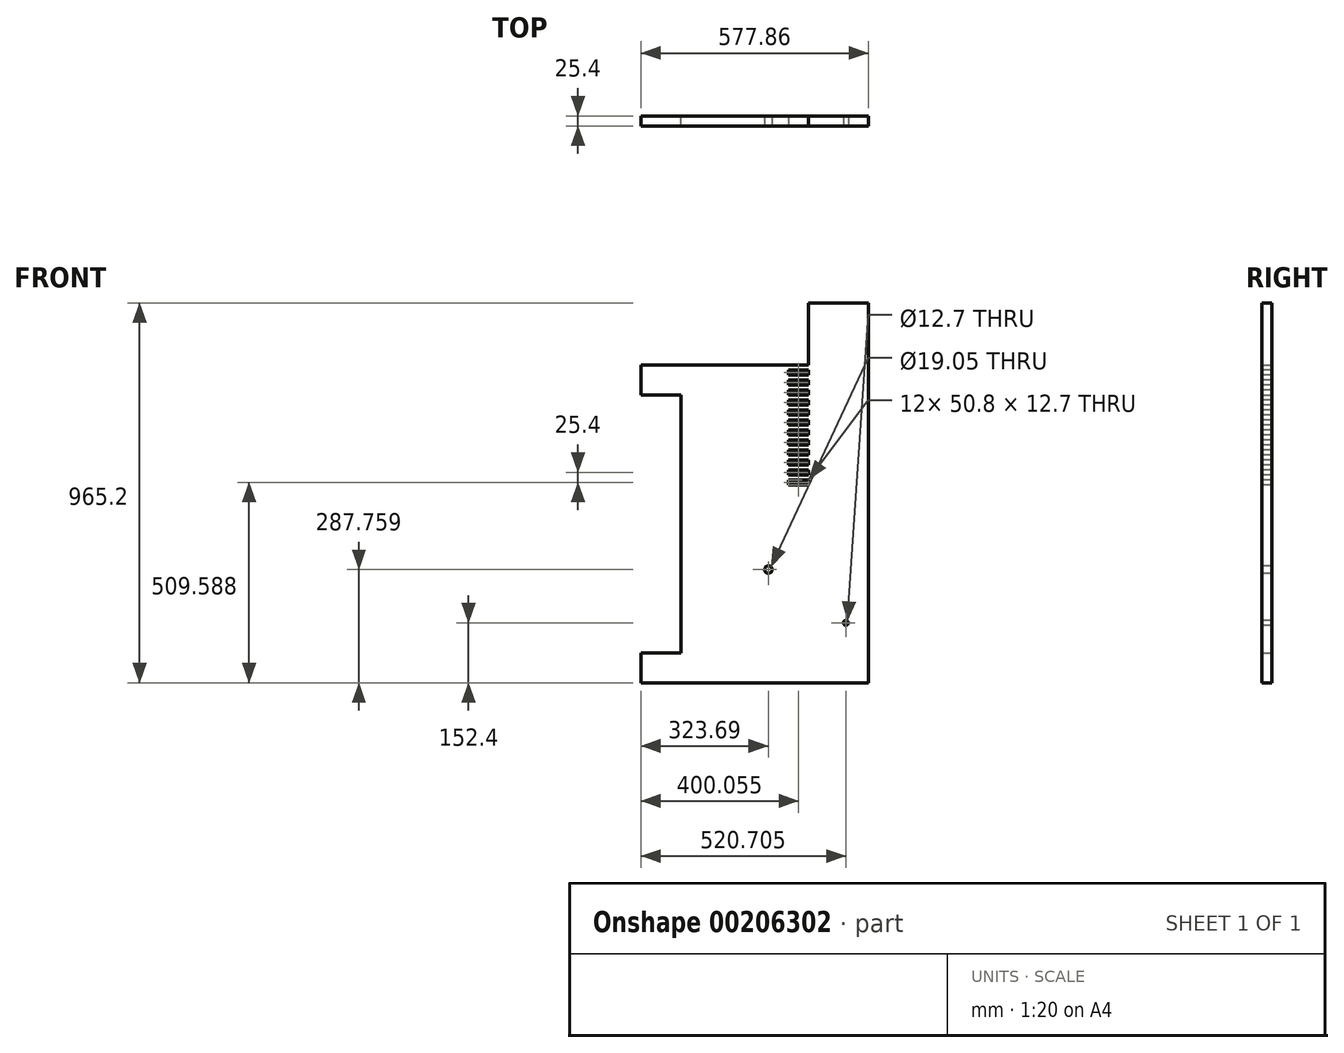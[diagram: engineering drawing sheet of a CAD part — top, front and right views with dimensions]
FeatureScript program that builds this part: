
annotation { "Feature Type Name" : "Feature", "Feature Type Description" : "" }
export const myFeature = defineFeature(function(context is Context, id is Id, definition is map)
    precondition{}
    {
        {
            var Q0;
            Q0=qCreatedBy(makeId("Front.planeOp"),FACE);
            var sketch = newSketch(context, id + "F0", { "sketchPlane" : qUnion([Q0])});
            skLineSegment(sketch, "E0.bottom", {"start": v(-288.93, 482.6) * mm, "end": v(288.93, 482.6) * mm, "construction": true});
            skLineSegment(sketch, "E0.top", {"start": v(-288.93, -482.6) * mm, "end": v(288.93, -482.6) * mm});
            skLineSegment(sketch, "E0.left", {"start": v(-288.92, 482.6) * mm, "end": v(-288.93, -482.6) * mm, "construction": true});
            skLineSegment(sketch, "E0.right", {"start": v(288.93, 482.6) * mm, "end": v(288.93, -482.6) * mm});
            skPoint(sketch, "E0.middle", {"position": v(0, 0) * mm});
            skLineSegment(sketch, "E1", {"start": v(136.52, 482.6) * mm, "end": v(288.93, 482.6) * mm});
            skLineSegment(sketch, "E2", {"start": v(136.52, 482.6) * mm, "end": v(136.53, 325.44) * mm});
            skLineSegment(sketch, "E3", {"start": v(136.53, 325.44) * mm, "end": v(-288.93, 325.44) * mm});
            skLineSegment(sketch, "E4", {"start": v(-288.93, 325.44) * mm, "end": v(-288.93, 249.24) * mm});
            skLineSegment(sketch, "E5", {"start": v(-288.93, 249.24) * mm, "end": v(-187.32, 249.24) * mm});
            skLineSegment(sketch, "E6", {"start": v(-187.32, 249.24) * mm, "end": v(-187.33, -406.4) * mm});
            skLineSegment(sketch, "E7", {"start": v(-187.33, -406.4) * mm, "end": v(-288.93, -406.4) * mm});
            skLineSegment(sketch, "E8", {"start": v(-288.93, -406.4) * mm, "end": v(-288.93, -482.6) * mm});
            skSolve(sketch);
        }
        {
            var Q0;
            Q0=makeQuery(id+"F0.imprint","IMPRINT",FACE,{"disambiguationData":[TD([[makeQuery(id+"F0.imprint","IMPRINT",EDGE,{"derivedFrom":sQuery(id+"F0.wireOp",EDGE,"E0.top")}),1.0]])]});
            extrude(context, id + "F1", {"entities" : qUnion([Q0]), "endBound" : BoundingType.SYMMETRIC, "depth" : 25.4 * mm});
        }
        {
            var Q0;
            Q0=makeQuery(id+"F1.opExtrude","CAP_FACE",FACE,{"disambiguationData":[OSD([sQuery(id+"F0.wireOp",EDGE,"E0.top"),sQuery(id+"F0.wireOp",EDGE,"E0.right"),sQuery(id+"F0.wireOp",EDGE,"E1"),sQuery(id+"F0.wireOp",EDGE,"E2"),sQuery(id+"F0.wireOp",EDGE,"E3"),sQuery(id+"F0.wireOp",EDGE,"E4"),sQuery(id+"F0.wireOp",EDGE,"E5"),sQuery(id+"F0.wireOp",EDGE,"E6"),sQuery(id+"F0.wireOp",EDGE,"E7"),sQuery(id+"F0.wireOp",EDGE,"E8")])],"isStart":false});
            var sketch = newSketch(context, id + "F2", { "sketchPlane" : qUnion([Q0])});
            skLineSegment(sketch, "E9", {"start": v(136.53, 325.44) * mm, "end": v(136.53, -482.6) * mm, "construction": true});
            skCircle(sketch, "E10", {"center": v(231.78, -330.2) * mm, "radius": 6.35 * mm});
            skSolve(sketch);
        }
        {
            var Q0;
            Q0 = qSketchRegion(id + "F2", true);
            extrude(context, id + "F3", {"entities" : qUnion([Q0]), "operationType" : NewBodyOperationType.REMOVE, "oppositeDirection" : true, "depth" : 25.4 * mm});
        }
        {
            var Q0;
            Q0=makeQuery(id+"F1.opExtrude","CAP_FACE",FACE,{"disambiguationData":[OSD([sQuery(id+"F0.wireOp",EDGE,"E0.top"),sQuery(id+"F0.wireOp",EDGE,"E0.right"),sQuery(id+"F0.wireOp",EDGE,"E1"),sQuery(id+"F0.wireOp",EDGE,"E2"),sQuery(id+"F0.wireOp",EDGE,"E3"),sQuery(id+"F0.wireOp",EDGE,"E4"),sQuery(id+"F0.wireOp",EDGE,"E5"),sQuery(id+"F0.wireOp",EDGE,"E6"),sQuery(id+"F0.wireOp",EDGE,"E7"),sQuery(id+"F0.wireOp",EDGE,"E8")])],"isStart":false});
            var sketch = newSketch(context, id + "F4", { "sketchPlane" : qUnion([Q0])});
            skLineSegment(sketch, "E11", {"start": v(-187.32, -330.2) * mm, "end": v(231.78, -330.2) * mm, "construction": true});
            skLineSegment(sketch, "E12", {"start": v(231.78, -330.2) * mm, "end": v(-187.33, -198.06) * mm, "construction": true});
            skLineSegment(sketch, "E13", {"start": v(-187.33, -124.82) * mm, "end": v(288.93, -274.98) * mm, "construction": true});
            skCircle(sketch, "E14", {"center": v(34.76, -194.84) * mm, "radius": 9.53 * mm});
            skLineSegment(sketch, "E15", {"start": v(34.76, -194.84) * mm, "end": v(13.76, -261.46) * mm, "construction": true});
            skLineSegment(sketch, "E16", {"start": v(231.78, -330.2) * mm, "end": v(252.78, -263.58) * mm, "construction": true});
            skSolve(sketch);
        }
        {
            var Q0;
            Q0 = qSketchRegion(id + "F4", true);
            extrude(context, id + "F5", {"entities" : qUnion([Q0]), "operationType" : NewBodyOperationType.REMOVE, "oppositeDirection" : true, "depth" : 25.4 * mm});
        }
        {
            var Q0;
            Q0=makeQuery(id+"F1.opExtrude","CAP_FACE",FACE,{"disambiguationData":[OSD([sQuery(id+"F0.wireOp",EDGE,"E0.top"),sQuery(id+"F0.wireOp",EDGE,"E0.right"),sQuery(id+"F0.wireOp",EDGE,"E1"),sQuery(id+"F0.wireOp",EDGE,"E2"),sQuery(id+"F0.wireOp",EDGE,"E3"),sQuery(id+"F0.wireOp",EDGE,"E4"),sQuery(id+"F0.wireOp",EDGE,"E5"),sQuery(id+"F0.wireOp",EDGE,"E6"),sQuery(id+"F0.wireOp",EDGE,"E7"),sQuery(id+"F0.wireOp",EDGE,"E8")])],"isStart":false});
            var sketch = newSketch(context, id + "F6", { "sketchPlane" : qUnion([Q0])});
            skLineSegment(sketch, "E17.bottom", {"start": v(85.72, 312.74) * mm, "end": v(136.53, 312.74) * mm});
            skLineSegment(sketch, "E17.top", {"start": v(85.72, 300.04) * mm, "end": v(136.53, 300.04) * mm});
            skLineSegment(sketch, "E17.left", {"start": v(85.72, 312.74) * mm, "end": v(85.72, 300.04) * mm});
            skLineSegment(sketch, "E17.right", {"start": v(136.53, 312.74) * mm, "end": v(136.53, 300.04) * mm});
            skLineSegment(sketch, "E18.0.1.0", {"start": v(136.53, 287.34) * mm, "end": v(136.53, 274.64) * mm});
            skLineSegment(sketch, "E18.0.1.1", {"start": v(85.72, 274.64) * mm, "end": v(136.53, 274.64) * mm});
            skLineSegment(sketch, "E18.0.1.2", {"start": v(85.72, 287.34) * mm, "end": v(85.72, 274.64) * mm});
            skLineSegment(sketch, "E18.0.1.3", {"start": v(85.72, 287.34) * mm, "end": v(136.53, 287.34) * mm});
            skLineSegment(sketch, "E18.0.2.0", {"start": v(136.53, 261.94) * mm, "end": v(136.53, 249.24) * mm});
            skLineSegment(sketch, "E18.0.2.1", {"start": v(85.72, 249.24) * mm, "end": v(136.53, 249.24) * mm});
            skLineSegment(sketch, "E18.0.2.2", {"start": v(85.72, 261.94) * mm, "end": v(85.72, 249.24) * mm});
            skLineSegment(sketch, "E18.0.2.3", {"start": v(85.72, 261.94) * mm, "end": v(136.53, 261.94) * mm});
            skLineSegment(sketch, "E18.0.3.0", {"start": v(136.53, 236.54) * mm, "end": v(136.53, 223.84) * mm});
            skLineSegment(sketch, "E18.0.3.1", {"start": v(85.72, 223.84) * mm, "end": v(136.53, 223.84) * mm});
            skLineSegment(sketch, "E18.0.3.2", {"start": v(85.72, 236.54) * mm, "end": v(85.72, 223.84) * mm});
            skLineSegment(sketch, "E18.0.3.3", {"start": v(85.72, 236.54) * mm, "end": v(136.53, 236.54) * mm});
            skLineSegment(sketch, "E18.0.4.0", {"start": v(136.53, 211.14) * mm, "end": v(136.53, 198.44) * mm});
            skLineSegment(sketch, "E18.0.4.1", {"start": v(85.72, 198.44) * mm, "end": v(136.53, 198.44) * mm});
            skLineSegment(sketch, "E18.0.4.2", {"start": v(85.72, 211.14) * mm, "end": v(85.72, 198.44) * mm});
            skLineSegment(sketch, "E18.0.4.3", {"start": v(85.72, 211.14) * mm, "end": v(136.53, 211.14) * mm});
            skLineSegment(sketch, "E18.0.5.0", {"start": v(136.53, 185.74) * mm, "end": v(136.53, 173.04) * mm});
            skLineSegment(sketch, "E18.0.5.1", {"start": v(85.72, 173.04) * mm, "end": v(136.53, 173.04) * mm});
            skLineSegment(sketch, "E18.0.5.2", {"start": v(85.72, 185.74) * mm, "end": v(85.72, 173.04) * mm});
            skLineSegment(sketch, "E18.0.5.3", {"start": v(85.72, 185.74) * mm, "end": v(136.53, 185.74) * mm});
            skLineSegment(sketch, "E18.0.6.0", {"start": v(136.53, 160.34) * mm, "end": v(136.53, 147.64) * mm});
            skLineSegment(sketch, "E18.0.6.1", {"start": v(85.72, 147.64) * mm, "end": v(136.53, 147.64) * mm});
            skLineSegment(sketch, "E18.0.6.2", {"start": v(85.72, 160.34) * mm, "end": v(85.72, 147.64) * mm});
            skLineSegment(sketch, "E18.0.6.3", {"start": v(85.72, 160.34) * mm, "end": v(136.53, 160.34) * mm});
            skLineSegment(sketch, "E18.0.7.0", {"start": v(136.53, 134.94) * mm, "end": v(136.53, 122.24) * mm});
            skLineSegment(sketch, "E18.0.7.1", {"start": v(85.72, 122.24) * mm, "end": v(136.53, 122.24) * mm});
            skLineSegment(sketch, "E18.0.7.2", {"start": v(85.72, 134.94) * mm, "end": v(85.72, 122.24) * mm});
            skLineSegment(sketch, "E18.0.7.3", {"start": v(85.72, 134.94) * mm, "end": v(136.53, 134.94) * mm});
            skLineSegment(sketch, "E18.0.8.0", {"start": v(136.53, 109.54) * mm, "end": v(136.53, 96.84) * mm});
            skLineSegment(sketch, "E18.0.8.1", {"start": v(85.72, 96.84) * mm, "end": v(136.53, 96.84) * mm});
            skLineSegment(sketch, "E18.0.8.2", {"start": v(85.72, 109.54) * mm, "end": v(85.72, 96.84) * mm});
            skLineSegment(sketch, "E18.0.8.3", {"start": v(85.72, 109.54) * mm, "end": v(136.53, 109.54) * mm});
            skLineSegment(sketch, "E18.0.9.0", {"start": v(136.53, 84.14) * mm, "end": v(136.53, 71.44) * mm});
            skLineSegment(sketch, "E18.0.9.1", {"start": v(85.72, 71.44) * mm, "end": v(136.53, 71.44) * mm});
            skLineSegment(sketch, "E18.0.9.2", {"start": v(85.72, 84.14) * mm, "end": v(85.72, 71.44) * mm});
            skLineSegment(sketch, "E18.0.9.3", {"start": v(85.72, 84.14) * mm, "end": v(136.53, 84.14) * mm});
            skLineSegment(sketch, "E18.0.10.0", {"start": v(136.53, 58.74) * mm, "end": v(136.53, 46.04) * mm});
            skLineSegment(sketch, "E18.0.10.1", {"start": v(85.72, 46.04) * mm, "end": v(136.53, 46.04) * mm});
            skLineSegment(sketch, "E18.0.10.2", {"start": v(85.72, 58.74) * mm, "end": v(85.72, 46.04) * mm});
            skLineSegment(sketch, "E18.0.10.3", {"start": v(85.72, 58.74) * mm, "end": v(136.53, 58.74) * mm});
            skLineSegment(sketch, "E18.0.11.0", {"start": v(136.53, 33.34) * mm, "end": v(136.53, 20.64) * mm});
            skLineSegment(sketch, "E18.0.11.1", {"start": v(85.72, 20.64) * mm, "end": v(136.53, 20.64) * mm});
            skLineSegment(sketch, "E18.0.11.2", {"start": v(85.72, 33.34) * mm, "end": v(85.72, 20.64) * mm});
            skLineSegment(sketch, "E18.0.11.3", {"start": v(85.72, 33.34) * mm, "end": v(136.53, 33.34) * mm});
            skLineSegment(sketch, "E18.direction1", {"start": v(136.53, 300.04) * mm, "end": v(161.93, 300.04) * mm, "construction": true});
            skLineSegment(sketch, "E18.direction2", {"start": v(136.53, 300.04) * mm, "end": v(136.53, 274.64) * mm, "construction": true});
            skSolve(sketch);
        }
        {
            var Q0;
            Q0 = qSketchRegion(id + "F6", true);
            extrude(context, id + "F7", {"entities" : qUnion([Q0]), "operationType" : NewBodyOperationType.REMOVE, "oppositeDirection" : true, "depth" : 25.4 * mm});
        }
    });
